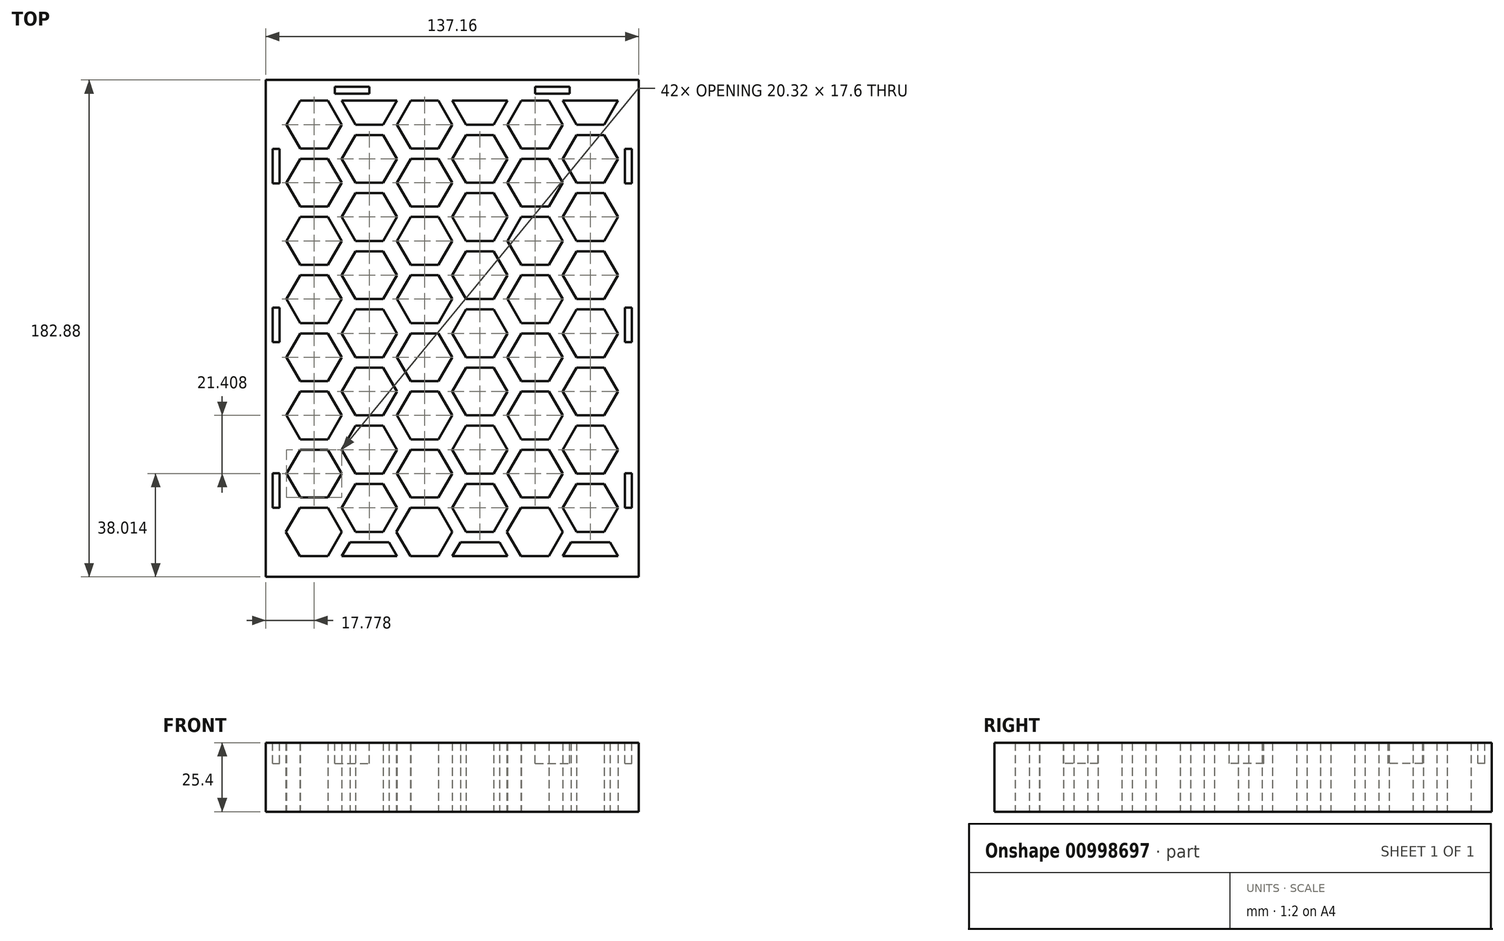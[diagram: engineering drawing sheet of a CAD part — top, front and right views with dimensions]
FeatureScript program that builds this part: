
annotation { "Feature Type Name" : "Feature", "Feature Type Description" : "" }
export const myFeature = defineFeature(function(context is Context, id is Id, definition is map)
    precondition{}
    {
        {
            var Q0;
            Q0=qCreatedBy(makeId("Top.planeOp"),FACE);
            var sketch = newSketch(context, id + "F0", { "sketchPlane" : qUnion([Q0])});
            skLineSegment(sketch, "E0", {"start": v(-64.11, 107.37) * mm, "end": v(-69.2, 98.57) * mm});
            skLineSegment(sketch, "E1", {"start": v(-69.2, 98.57) * mm, "end": v(-64.11, 89.77) * mm});
            skLineSegment(sketch, "E2", {"start": v(-64.11, 89.77) * mm, "end": v(-53.95, 89.77) * mm});
            skLineSegment(sketch, "E3", {"start": v(-53.95, 89.77) * mm, "end": v(-48.87, 98.57) * mm});
            skLineSegment(sketch, "E4", {"start": v(-48.87, 98.57) * mm, "end": v(-53.95, 107.37) * mm});
            skLineSegment(sketch, "E5", {"start": v(-53.95, 107.37) * mm, "end": v(-64.11, 107.37) * mm});
            skLineSegment(sketch, "E6", {"start": v(-64.28, -42.48) * mm, "end": v(-69.41, -51.38) * mm});
            skLineSegment(sketch, "E7", {"start": v(-69.41, -51.38) * mm, "end": v(-64.28, -60.27) * mm});
            skLineSegment(sketch, "E8", {"start": v(-64.28, -60.27) * mm, "end": v(-54, -60.27) * mm});
            skLineSegment(sketch, "E9", {"start": v(-54, -60.27) * mm, "end": v(-48.87, -51.38) * mm});
            skLineSegment(sketch, "E10", {"start": v(-48.87, -51.38) * mm, "end": v(-54, -42.48) * mm});
            skLineSegment(sketch, "E11", {"start": v(-54, -42.48) * mm, "end": v(-64.28, -42.48) * mm});
            skLineSegment(sketch, "E12", {"start": v(-48.87, 107.37) * mm, "end": v(-43.8, 98.57) * mm});
            skLineSegment(sketch, "E13", {"start": v(-43.8, 98.57) * mm, "end": v(-33.63, 98.57) * mm});
            skLineSegment(sketch, "E14", {"start": v(-33.63, 98.57) * mm, "end": v(-28.55, 107.37) * mm});
            skLineSegment(sketch, "E15", {"start": v(-48.87, 107.37) * mm, "end": v(-48.87, -60.27) * mm, "construction": true});
            skLineSegment(sketch, "E16", {"start": v(-43.8, 94.76) * mm, "end": v(-48.87, 85.96) * mm});
            skLineSegment(sketch, "E17", {"start": v(-48.87, 85.96) * mm, "end": v(-43.8, 77.16) * mm});
            skLineSegment(sketch, "E18", {"start": v(-43.8, 77.16) * mm, "end": v(-33.63, 77.16) * mm});
            skLineSegment(sketch, "E19", {"start": v(-33.63, 77.16) * mm, "end": v(-28.55, 85.96) * mm});
            skLineSegment(sketch, "E20", {"start": v(-28.55, 85.96) * mm, "end": v(-33.63, 94.76) * mm});
            skLineSegment(sketch, "E21", {"start": v(-33.63, 94.76) * mm, "end": v(-43.8, 94.76) * mm});
            skLineSegment(sketch, "E22", {"start": v(-43.8, 73.35) * mm, "end": v(-48.87, 64.55) * mm});
            skLineSegment(sketch, "E23", {"start": v(-48.87, 64.55) * mm, "end": v(-43.8, 55.76) * mm});
            skLineSegment(sketch, "E24", {"start": v(-43.8, 55.76) * mm, "end": v(-33.63, 55.76) * mm});
            skLineSegment(sketch, "E25", {"start": v(-33.63, 55.76) * mm, "end": v(-28.55, 64.55) * mm});
            skLineSegment(sketch, "E26", {"start": v(-28.55, 64.55) * mm, "end": v(-33.63, 73.35) * mm});
            skLineSegment(sketch, "E27", {"start": v(-33.63, 73.35) * mm, "end": v(-43.8, 73.35) * mm});
            skLineSegment(sketch, "E28", {"start": v(-43.8, 51.95) * mm, "end": v(-48.87, 43.15) * mm});
            skLineSegment(sketch, "E29", {"start": v(-48.87, 43.15) * mm, "end": v(-43.8, 34.35) * mm});
            skLineSegment(sketch, "E30", {"start": v(-43.8, 34.35) * mm, "end": v(-33.63, 34.35) * mm});
            skLineSegment(sketch, "E31", {"start": v(-33.63, 34.35) * mm, "end": v(-28.55, 43.15) * mm});
            skLineSegment(sketch, "E32", {"start": v(-28.55, 43.15) * mm, "end": v(-33.63, 51.95) * mm});
            skLineSegment(sketch, "E33", {"start": v(-33.63, 51.95) * mm, "end": v(-43.8, 51.95) * mm});
            skLineSegment(sketch, "E34", {"start": v(-43.8, 30.54) * mm, "end": v(-48.87, 21.74) * mm});
            skLineSegment(sketch, "E35", {"start": v(-48.87, 21.74) * mm, "end": v(-43.8, 12.94) * mm});
            skLineSegment(sketch, "E36", {"start": v(-43.8, 12.94) * mm, "end": v(-33.63, 12.94) * mm});
            skLineSegment(sketch, "E37", {"start": v(-33.63, 12.94) * mm, "end": v(-28.55, 21.74) * mm});
            skLineSegment(sketch, "E38", {"start": v(-28.55, 21.74) * mm, "end": v(-33.63, 30.54) * mm});
            skLineSegment(sketch, "E39", {"start": v(-33.63, 30.54) * mm, "end": v(-43.8, 30.54) * mm});
            skLineSegment(sketch, "E40", {"start": v(-43.8, 9.13) * mm, "end": v(-48.87, 0.33) * mm});
            skLineSegment(sketch, "E41", {"start": v(-48.87, 0.33) * mm, "end": v(-43.8, -8.47) * mm});
            skLineSegment(sketch, "E42", {"start": v(-43.8, -8.47) * mm, "end": v(-33.63, -8.47) * mm});
            skLineSegment(sketch, "E43", {"start": v(-33.63, -8.47) * mm, "end": v(-28.55, 0.33) * mm});
            skLineSegment(sketch, "E44", {"start": v(-28.55, 0.33) * mm, "end": v(-33.63, 9.13) * mm});
            skLineSegment(sketch, "E45", {"start": v(-33.63, 9.13) * mm, "end": v(-43.8, 9.13) * mm});
            skLineSegment(sketch, "E46", {"start": v(-43.8, -12.28) * mm, "end": v(-48.87, -21.08) * mm});
            skLineSegment(sketch, "E47", {"start": v(-48.87, -21.08) * mm, "end": v(-43.8, -29.88) * mm});
            skLineSegment(sketch, "E48", {"start": v(-43.8, -29.88) * mm, "end": v(-33.63, -29.88) * mm});
            skLineSegment(sketch, "E49", {"start": v(-33.63, -29.88) * mm, "end": v(-28.55, -21.08) * mm});
            skLineSegment(sketch, "E50", {"start": v(-28.55, -21.08) * mm, "end": v(-33.63, -12.28) * mm});
            skLineSegment(sketch, "E51", {"start": v(-33.63, -12.28) * mm, "end": v(-43.8, -12.28) * mm});
            skLineSegment(sketch, "E52", {"start": v(-43.8, -33.69) * mm, "end": v(-48.87, -42.48) * mm});
            skLineSegment(sketch, "E53", {"start": v(-48.87, -42.48) * mm, "end": v(-43.8, -51.28) * mm});
            skLineSegment(sketch, "E54", {"start": v(-43.8, -51.28) * mm, "end": v(-33.63, -51.28) * mm});
            skLineSegment(sketch, "E55", {"start": v(-33.63, -51.28) * mm, "end": v(-28.55, -42.48) * mm});
            skLineSegment(sketch, "E56", {"start": v(-28.55, -42.48) * mm, "end": v(-33.63, -33.69) * mm});
            skLineSegment(sketch, "E57", {"start": v(-33.63, -33.69) * mm, "end": v(-43.8, -33.69) * mm});
            skLineSegment(sketch, "E58", {"start": v(-45.88, -55.1) * mm, "end": v(-48.87, -60.27) * mm});
            skLineSegment(sketch, "E59", {"start": v(-28.55, -60.27) * mm, "end": v(-31.54, -55.1) * mm});
            skLineSegment(sketch, "E60", {"start": v(-31.54, -55.1) * mm, "end": v(-45.88, -55.1) * mm});
            skLineSegment(sketch, "E61", {"start": v(-28.55, 107.37) * mm, "end": v(-28.55, -60.27) * mm, "construction": true});
            skLineSegment(sketch, "E62", {"start": v(-23.47, 107.37) * mm, "end": v(-28.55, 98.57) * mm});
            skLineSegment(sketch, "E63", {"start": v(-28.55, 98.57) * mm, "end": v(-23.47, 89.77) * mm});
            skLineSegment(sketch, "E64", {"start": v(-23.47, 89.77) * mm, "end": v(-13.31, 89.77) * mm});
            skLineSegment(sketch, "E65", {"start": v(-13.31, 89.77) * mm, "end": v(-8.23, 98.57) * mm});
            skLineSegment(sketch, "E66", {"start": v(-8.23, 98.57) * mm, "end": v(-13.31, 107.37) * mm});
            skLineSegment(sketch, "E67", {"start": v(-13.31, 107.37) * mm, "end": v(-23.47, 107.37) * mm});
            skLineSegment(sketch, "E68", {"start": v(-23.47, 85.96) * mm, "end": v(-28.55, 77.16) * mm});
            skLineSegment(sketch, "E69", {"start": v(-28.55, 77.16) * mm, "end": v(-23.47, 68.36) * mm});
            skLineSegment(sketch, "E70", {"start": v(-23.47, 68.36) * mm, "end": v(-13.31, 68.36) * mm});
            skLineSegment(sketch, "E71", {"start": v(-13.31, 68.36) * mm, "end": v(-8.23, 77.16) * mm});
            skLineSegment(sketch, "E72", {"start": v(-8.23, 77.16) * mm, "end": v(-13.31, 85.96) * mm});
            skLineSegment(sketch, "E73", {"start": v(-13.31, 85.96) * mm, "end": v(-23.47, 85.96) * mm});
            skLineSegment(sketch, "E74", {"start": v(-23.47, 43.15) * mm, "end": v(-28.55, 34.35) * mm});
            skLineSegment(sketch, "E75", {"start": v(-28.55, 34.35) * mm, "end": v(-23.47, 25.55) * mm});
            skLineSegment(sketch, "E76", {"start": v(-23.47, 25.55) * mm, "end": v(-13.31, 25.55) * mm});
            skLineSegment(sketch, "E77", {"start": v(-13.31, 25.55) * mm, "end": v(-8.23, 34.35) * mm});
            skLineSegment(sketch, "E78", {"start": v(-8.23, 34.35) * mm, "end": v(-13.31, 43.15) * mm});
            skLineSegment(sketch, "E79", {"start": v(-13.31, 43.15) * mm, "end": v(-23.47, 43.15) * mm});
            skLineSegment(sketch, "E80", {"start": v(-23.47, 21.74) * mm, "end": v(-28.55, 12.94) * mm});
            skLineSegment(sketch, "E81", {"start": v(-28.55, 12.94) * mm, "end": v(-23.47, 4.14) * mm});
            skLineSegment(sketch, "E82", {"start": v(-23.47, 4.14) * mm, "end": v(-13.31, 4.14) * mm});
            skLineSegment(sketch, "E83", {"start": v(-13.31, 4.14) * mm, "end": v(-8.23, 12.94) * mm});
            skLineSegment(sketch, "E84", {"start": v(-8.23, 12.94) * mm, "end": v(-13.31, 21.74) * mm});
            skLineSegment(sketch, "E85", {"start": v(-13.31, 21.74) * mm, "end": v(-23.47, 21.74) * mm});
            skLineSegment(sketch, "E86", {"start": v(-23.47, 64.55) * mm, "end": v(-28.55, 55.76) * mm});
            skLineSegment(sketch, "E87", {"start": v(-28.55, 55.76) * mm, "end": v(-23.47, 46.96) * mm});
            skLineSegment(sketch, "E88", {"start": v(-23.47, 46.96) * mm, "end": v(-13.31, 46.96) * mm});
            skLineSegment(sketch, "E89", {"start": v(-13.31, 46.96) * mm, "end": v(-8.23, 55.76) * mm});
            skLineSegment(sketch, "E90", {"start": v(-8.23, 55.76) * mm, "end": v(-13.31, 64.55) * mm});
            skLineSegment(sketch, "E91", {"start": v(-13.31, 64.55) * mm, "end": v(-23.47, 64.55) * mm});
            skLineSegment(sketch, "E92", {"start": v(-23.47, 0.33) * mm, "end": v(-28.55, -8.47) * mm});
            skLineSegment(sketch, "E93", {"start": v(-28.55, -8.47) * mm, "end": v(-23.47, -17.27) * mm});
            skLineSegment(sketch, "E94", {"start": v(-23.47, -17.27) * mm, "end": v(-13.31, -17.27) * mm});
            skLineSegment(sketch, "E95", {"start": v(-13.31, -17.27) * mm, "end": v(-8.23, -8.47) * mm});
            skLineSegment(sketch, "E96", {"start": v(-8.23, -8.47) * mm, "end": v(-13.31, 0.33) * mm});
            skLineSegment(sketch, "E97", {"start": v(-13.31, 0.33) * mm, "end": v(-23.47, 0.33) * mm});
            skLineSegment(sketch, "E98", {"start": v(-23.47, -21.08) * mm, "end": v(-28.55, -29.88) * mm});
            skLineSegment(sketch, "E99", {"start": v(-28.55, -29.88) * mm, "end": v(-23.47, -38.67) * mm});
            skLineSegment(sketch, "E100", {"start": v(-23.47, -38.67) * mm, "end": v(-13.31, -38.67) * mm});
            skLineSegment(sketch, "E101", {"start": v(-13.31, -38.67) * mm, "end": v(-8.23, -29.88) * mm});
            skLineSegment(sketch, "E102", {"start": v(-8.23, -29.88) * mm, "end": v(-13.31, -21.08) * mm});
            skLineSegment(sketch, "E103", {"start": v(-13.31, -21.08) * mm, "end": v(-23.47, -21.08) * mm});
            skLineSegment(sketch, "E104", {"start": v(-23.64, -42.48) * mm, "end": v(-28.77, -51.38) * mm});
            skLineSegment(sketch, "E105", {"start": v(-28.77, -51.38) * mm, "end": v(-23.64, -60.27) * mm});
            skLineSegment(sketch, "E106", {"start": v(-23.64, -60.27) * mm, "end": v(-13.37, -60.27) * mm});
            skLineSegment(sketch, "E107", {"start": v(-13.37, -60.27) * mm, "end": v(-8.23, -51.38) * mm});
            skLineSegment(sketch, "E108", {"start": v(-8.23, -51.38) * mm, "end": v(-13.37, -42.48) * mm});
            skLineSegment(sketch, "E109", {"start": v(-13.37, -42.48) * mm, "end": v(-23.64, -42.48) * mm});
            skLineSegment(sketch, "E110", {"start": v(-8.23, 107.37) * mm, "end": v(-3.15, 98.57) * mm});
            skLineSegment(sketch, "E111", {"start": v(-3.15, 98.57) * mm, "end": v(7, 98.57) * mm});
            skLineSegment(sketch, "E112", {"start": v(7, 98.57) * mm, "end": v(12.09, 107.37) * mm});
            skLineSegment(sketch, "E113", {"start": v(-8.23, 107.37) * mm, "end": v(-8.23, -60.27) * mm, "construction": true});
            skLineSegment(sketch, "E114", {"start": v(-3.15, 94.76) * mm, "end": v(-8.23, 85.96) * mm});
            skLineSegment(sketch, "E115", {"start": v(-8.23, 85.96) * mm, "end": v(-3.15, 77.16) * mm});
            skLineSegment(sketch, "E116", {"start": v(-3.15, 77.16) * mm, "end": v(7, 77.16) * mm});
            skLineSegment(sketch, "E117", {"start": v(7, 77.16) * mm, "end": v(12.09, 85.96) * mm});
            skLineSegment(sketch, "E118", {"start": v(12.09, 85.96) * mm, "end": v(7, 94.76) * mm});
            skLineSegment(sketch, "E119", {"start": v(7, 94.76) * mm, "end": v(-3.15, 94.76) * mm});
            skLineSegment(sketch, "E120", {"start": v(-3.15, 73.35) * mm, "end": v(-8.23, 64.55) * mm});
            skLineSegment(sketch, "E121", {"start": v(-8.23, 64.55) * mm, "end": v(-3.15, 55.76) * mm});
            skLineSegment(sketch, "E122", {"start": v(-3.15, 55.76) * mm, "end": v(7, 55.76) * mm});
            skLineSegment(sketch, "E123", {"start": v(7, 55.76) * mm, "end": v(12.09, 64.55) * mm});
            skLineSegment(sketch, "E124", {"start": v(12.09, 64.55) * mm, "end": v(7, 73.35) * mm});
            skLineSegment(sketch, "E125", {"start": v(7, 73.35) * mm, "end": v(-3.15, 73.35) * mm});
            skLineSegment(sketch, "E126", {"start": v(-3.15, 51.95) * mm, "end": v(-8.23, 43.15) * mm});
            skLineSegment(sketch, "E127", {"start": v(-8.23, 43.15) * mm, "end": v(-3.15, 34.35) * mm});
            skLineSegment(sketch, "E128", {"start": v(-3.15, 34.35) * mm, "end": v(7, 34.35) * mm});
            skLineSegment(sketch, "E129", {"start": v(7, 34.35) * mm, "end": v(12.09, 43.15) * mm});
            skLineSegment(sketch, "E130", {"start": v(12.09, 43.15) * mm, "end": v(7, 51.95) * mm});
            skLineSegment(sketch, "E131", {"start": v(7, 51.95) * mm, "end": v(-3.15, 51.95) * mm});
            skLineSegment(sketch, "E132", {"start": v(-3.15, 30.54) * mm, "end": v(-8.23, 21.74) * mm});
            skLineSegment(sketch, "E133", {"start": v(-8.23, 21.74) * mm, "end": v(-3.15, 12.94) * mm});
            skLineSegment(sketch, "E134", {"start": v(-3.15, 12.94) * mm, "end": v(7, 12.94) * mm});
            skLineSegment(sketch, "E135", {"start": v(7, 12.94) * mm, "end": v(12.09, 21.74) * mm});
            skLineSegment(sketch, "E136", {"start": v(12.09, 21.74) * mm, "end": v(7, 30.54) * mm});
            skLineSegment(sketch, "E137", {"start": v(7, 30.54) * mm, "end": v(-3.15, 30.54) * mm});
            skLineSegment(sketch, "E138", {"start": v(-3.15, 9.13) * mm, "end": v(-8.23, 0.33) * mm});
            skLineSegment(sketch, "E139", {"start": v(-8.23, 0.33) * mm, "end": v(-3.15, -8.47) * mm});
            skLineSegment(sketch, "E140", {"start": v(-3.15, -8.47) * mm, "end": v(7, -8.47) * mm});
            skLineSegment(sketch, "E141", {"start": v(7, -8.47) * mm, "end": v(12.09, 0.33) * mm});
            skLineSegment(sketch, "E142", {"start": v(12.09, 0.33) * mm, "end": v(7, 9.13) * mm});
            skLineSegment(sketch, "E143", {"start": v(7, 9.13) * mm, "end": v(-3.15, 9.13) * mm});
            skLineSegment(sketch, "E144", {"start": v(-3.15, -12.28) * mm, "end": v(-8.23, -21.08) * mm});
            skLineSegment(sketch, "E145", {"start": v(-8.23, -21.08) * mm, "end": v(-3.15, -29.88) * mm});
            skLineSegment(sketch, "E146", {"start": v(-3.15, -29.88) * mm, "end": v(7, -29.88) * mm});
            skLineSegment(sketch, "E147", {"start": v(7, -29.88) * mm, "end": v(12.09, -21.08) * mm});
            skLineSegment(sketch, "E148", {"start": v(12.09, -21.08) * mm, "end": v(7, -12.28) * mm});
            skLineSegment(sketch, "E149", {"start": v(7, -12.28) * mm, "end": v(-3.15, -12.28) * mm});
            skLineSegment(sketch, "E150", {"start": v(-3.15, -33.69) * mm, "end": v(-8.23, -42.48) * mm});
            skLineSegment(sketch, "E151", {"start": v(-8.23, -42.48) * mm, "end": v(-3.15, -51.28) * mm});
            skLineSegment(sketch, "E152", {"start": v(-3.15, -51.28) * mm, "end": v(7, -51.28) * mm});
            skLineSegment(sketch, "E153", {"start": v(7, -51.28) * mm, "end": v(12.09, -42.48) * mm});
            skLineSegment(sketch, "E154", {"start": v(12.09, -42.48) * mm, "end": v(7, -33.69) * mm});
            skLineSegment(sketch, "E155", {"start": v(7, -33.69) * mm, "end": v(-3.15, -33.69) * mm});
            skLineSegment(sketch, "E156", {"start": v(-5.24, -55.1) * mm, "end": v(-8.23, -60.27) * mm});
            skLineSegment(sketch, "E157", {"start": v(12.09, -60.27) * mm, "end": v(9.1, -55.1) * mm});
            skLineSegment(sketch, "E158", {"start": v(9.1, -55.1) * mm, "end": v(-5.24, -55.1) * mm});
            skLineSegment(sketch, "E159", {"start": v(12.09, 107.37) * mm, "end": v(12.09, -60.27) * mm, "construction": true});
            skLineSegment(sketch, "E160", {"start": v(-69.2, 107.37) * mm, "end": v(52.73, 107.37) * mm, "construction": true});
            skLineSegment(sketch, "E161", {"start": v(17.17, 107.37) * mm, "end": v(12.09, 98.57) * mm});
            skLineSegment(sketch, "E162", {"start": v(12.09, 98.57) * mm, "end": v(17.17, 89.77) * mm});
            skLineSegment(sketch, "E163", {"start": v(17.17, 89.77) * mm, "end": v(27.33, 89.77) * mm});
            skLineSegment(sketch, "E164", {"start": v(27.33, 89.77) * mm, "end": v(32.4, 98.57) * mm});
            skLineSegment(sketch, "E165", {"start": v(32.4, 98.57) * mm, "end": v(27.33, 107.37) * mm});
            skLineSegment(sketch, "E166", {"start": v(27.33, 107.37) * mm, "end": v(17.17, 107.37) * mm});
            skLineSegment(sketch, "E167", {"start": v(17.17, 85.96) * mm, "end": v(12.09, 77.16) * mm});
            skLineSegment(sketch, "E168", {"start": v(12.09, 77.16) * mm, "end": v(17.17, 68.36) * mm});
            skLineSegment(sketch, "E169", {"start": v(17.17, 68.36) * mm, "end": v(27.33, 68.36) * mm});
            skLineSegment(sketch, "E170", {"start": v(27.33, 68.36) * mm, "end": v(32.4, 77.16) * mm});
            skLineSegment(sketch, "E171", {"start": v(32.4, 77.16) * mm, "end": v(27.33, 85.96) * mm});
            skLineSegment(sketch, "E172", {"start": v(27.33, 85.96) * mm, "end": v(17.17, 85.96) * mm});
            skLineSegment(sketch, "E173", {"start": v(17.17, 43.15) * mm, "end": v(12.09, 34.35) * mm});
            skLineSegment(sketch, "E174", {"start": v(12.09, 34.35) * mm, "end": v(17.17, 25.55) * mm});
            skLineSegment(sketch, "E175", {"start": v(17.17, 25.55) * mm, "end": v(27.33, 25.55) * mm});
            skLineSegment(sketch, "E176", {"start": v(27.33, 25.55) * mm, "end": v(32.4, 34.35) * mm});
            skLineSegment(sketch, "E177", {"start": v(32.4, 34.35) * mm, "end": v(27.33, 43.15) * mm});
            skLineSegment(sketch, "E178", {"start": v(27.33, 43.15) * mm, "end": v(17.17, 43.15) * mm});
            skLineSegment(sketch, "E179", {"start": v(17.17, 21.74) * mm, "end": v(12.09, 12.94) * mm});
            skLineSegment(sketch, "E180", {"start": v(12.09, 12.94) * mm, "end": v(17.17, 4.14) * mm});
            skLineSegment(sketch, "E181", {"start": v(17.17, 4.14) * mm, "end": v(27.33, 4.14) * mm});
            skLineSegment(sketch, "E182", {"start": v(27.33, 4.14) * mm, "end": v(32.4, 12.94) * mm});
            skLineSegment(sketch, "E183", {"start": v(32.4, 12.94) * mm, "end": v(27.33, 21.74) * mm});
            skLineSegment(sketch, "E184", {"start": v(27.33, 21.74) * mm, "end": v(17.17, 21.74) * mm});
            skLineSegment(sketch, "E185", {"start": v(17.17, 64.55) * mm, "end": v(12.09, 55.76) * mm});
            skLineSegment(sketch, "E186", {"start": v(12.09, 55.76) * mm, "end": v(17.17, 46.96) * mm});
            skLineSegment(sketch, "E187", {"start": v(17.17, 46.96) * mm, "end": v(27.33, 46.96) * mm});
            skLineSegment(sketch, "E188", {"start": v(27.33, 46.96) * mm, "end": v(32.4, 55.76) * mm});
            skLineSegment(sketch, "E189", {"start": v(32.4, 55.76) * mm, "end": v(27.33, 64.55) * mm});
            skLineSegment(sketch, "E190", {"start": v(27.33, 64.55) * mm, "end": v(17.17, 64.55) * mm});
            skLineSegment(sketch, "E191", {"start": v(17.17, 0.33) * mm, "end": v(12.09, -8.47) * mm});
            skLineSegment(sketch, "E192", {"start": v(12.09, -8.47) * mm, "end": v(17.17, -17.27) * mm});
            skLineSegment(sketch, "E193", {"start": v(17.17, -17.27) * mm, "end": v(27.33, -17.27) * mm});
            skLineSegment(sketch, "E194", {"start": v(27.33, -17.27) * mm, "end": v(32.4, -8.47) * mm});
            skLineSegment(sketch, "E195", {"start": v(32.4, -8.47) * mm, "end": v(27.33, 0.33) * mm});
            skLineSegment(sketch, "E196", {"start": v(27.33, 0.33) * mm, "end": v(17.17, 0.33) * mm});
            skLineSegment(sketch, "E197", {"start": v(17.17, -21.08) * mm, "end": v(12.09, -29.88) * mm});
            skLineSegment(sketch, "E198", {"start": v(12.09, -29.88) * mm, "end": v(17.17, -38.67) * mm});
            skLineSegment(sketch, "E199", {"start": v(17.17, -38.67) * mm, "end": v(27.33, -38.67) * mm});
            skLineSegment(sketch, "E200", {"start": v(27.33, -38.67) * mm, "end": v(32.4, -29.88) * mm});
            skLineSegment(sketch, "E201", {"start": v(32.4, -29.88) * mm, "end": v(27.33, -21.08) * mm});
            skLineSegment(sketch, "E202", {"start": v(27.33, -21.08) * mm, "end": v(17.17, -21.08) * mm});
            skLineSegment(sketch, "E203", {"start": v(17, -42.48) * mm, "end": v(11.87, -51.38) * mm});
            skLineSegment(sketch, "E204", {"start": v(11.87, -51.38) * mm, "end": v(17, -60.27) * mm});
            skLineSegment(sketch, "E205", {"start": v(17, -60.27) * mm, "end": v(27.27, -60.27) * mm});
            skLineSegment(sketch, "E206", {"start": v(27.27, -60.27) * mm, "end": v(32.4, -51.38) * mm});
            skLineSegment(sketch, "E207", {"start": v(32.4, -51.38) * mm, "end": v(27.27, -42.48) * mm});
            skLineSegment(sketch, "E208", {"start": v(27.27, -42.48) * mm, "end": v(17, -42.48) * mm});
            skLineSegment(sketch, "E209", {"start": v(32.4, 107.37) * mm, "end": v(37.49, 98.57) * mm});
            skLineSegment(sketch, "E210", {"start": v(37.49, 98.57) * mm, "end": v(47.65, 98.57) * mm});
            skLineSegment(sketch, "E211", {"start": v(47.65, 98.57) * mm, "end": v(52.73, 107.37) * mm});
            skLineSegment(sketch, "E212", {"start": v(32.4, 107.37) * mm, "end": v(32.4, -60.27) * mm, "construction": true});
            skLineSegment(sketch, "E213", {"start": v(35.4, -55.1) * mm, "end": v(32.4, -60.27) * mm});
            skLineSegment(sketch, "E214", {"start": v(52.73, -60.27) * mm, "end": v(49.74, -55.1) * mm});
            skLineSegment(sketch, "E215", {"start": v(49.74, -55.1) * mm, "end": v(35.4, -55.1) * mm});
            skLineSegment(sketch, "E216", {"start": v(52.73, 107.37) * mm, "end": v(52.73, -60.27) * mm, "construction": true});
            skLineSegment(sketch, "E217", {"start": v(52.73, -60.27) * mm, "end": v(-69.2, -60.27) * mm, "construction": true});
            skLineSegment(sketch, "E218", {"start": v(-69.2, -60.27) * mm, "end": v(-69.2, 107.37) * mm, "construction": true});
            skLineSegment(sketch, "E219.bottom", {"start": v(-76.81, 114.99) * mm, "end": v(60.35, 114.99) * mm});
            skLineSegment(sketch, "E219.top", {"start": v(-76.81, -67.9) * mm, "end": v(60.35, -67.9) * mm});
            skLineSegment(sketch, "E219.left", {"start": v(-76.81, 114.99) * mm, "end": v(-76.81, -67.9) * mm});
            skLineSegment(sketch, "E219.right", {"start": v(60.35, 114.99) * mm, "end": v(60.35, -67.9) * mm});
            skLineSegment(sketch, "E220.bottom", {"start": v(-73, 111.18) * mm, "end": v(56.54, 111.18) * mm});
            skLineSegment(sketch, "E220.top", {"start": v(-73, -67.9) * mm, "end": v(56.54, -67.9) * mm});
            skLineSegment(sketch, "E220.left", {"start": v(-73, 111.18) * mm, "end": v(-73, -67.9) * mm});
            skLineSegment(sketch, "E220.right", {"start": v(56.54, 111.18) * mm, "end": v(56.54, -67.9) * mm});
            skLineSegment(sketch, "E221", {"start": v(32.4, -60.27) * mm, "end": v(52.73, -60.27) * mm});
            skLineSegment(sketch, "E222", {"start": v(-8.23, -60.27) * mm, "end": v(12.09, -60.27) * mm});
            skLineSegment(sketch, "E223", {"start": v(32.4, 107.37) * mm, "end": v(52.73, 107.37) * mm});
            skLineSegment(sketch, "E224", {"start": v(12.09, 107.37) * mm, "end": v(-8.23, 107.37) * mm});
            skLineSegment(sketch, "E225", {"start": v(-28.55, 107.37) * mm, "end": v(-48.87, 107.37) * mm});
            skLineSegment(sketch, "E226", {"start": v(-48.87, -60.27) * mm, "end": v(-28.55, -60.27) * mm});
            skSolve(sketch);
        }
        {
            var Q0;
            Q0=makeQuery(id+"F0.imprint","IMPRINT",FACE,{"disambiguationData":[TD([[makeQuery(id+"F0.imprint","IMPRINT",EDGE,{"derivedFrom":sQuery(id+"F0.wireOp",EDGE,"a3d6729a-a9fa-40fb-8c57-60344376bb60")}),1.0]])]});
            var Q1;
            Q1=makeQuery(id+"F0.imprint","IMPRINT",FACE,{"disambiguationData":[TD([[makeQuery(id+"F0.imprint","IMPRINT",EDGE,{"derivedFrom":sQuery(id+"F0.wireOp",EDGE,"36840c81-68fc-456b-b918-5e75b1f56573")}),1.0]])]});
            var Q2;
            Q2=makeQuery(id+"F0.imprint","IMPRINT",FACE,{"disambiguationData":[TD([[makeQuery(id+"F0.imprint","IMPRINT",EDGE,{"derivedFrom":sQuery(id+"F0.wireOp",EDGE,"b8766c8d-9eda-4f00-b00c-fb24c00b1e0d")}),1.0]])]});
            var Q3;
            Q3=makeQuery(id+"F0.imprint","IMPRINT",FACE,{"disambiguationData":[TD([[makeQuery(id+"F0.imprint","IMPRINT",EDGE,{"derivedFrom":sQuery(id+"F0.wireOp",EDGE,"E28")}),1.0]])]});
            var Q4;
            Q4=makeQuery(id+"F0.imprint","IMPRINT",FACE,{"disambiguationData":[TD([[makeQuery(id+"F0.imprint","IMPRINT",EDGE,{"derivedFrom":sQuery(id+"F0.wireOp",EDGE,"E74")}),1.0]])]});
            var Q5;
            Q5=makeQuery(id+"F0.imprint","IMPRINT",FACE,{"disambiguationData":[TD([[makeQuery(id+"F0.imprint","IMPRINT",EDGE,{"derivedFrom":sQuery(id+"F0.wireOp",EDGE,"E80")}),1.0]])]});
            var Q6;
            Q6=makeQuery(id+"F0.imprint","IMPRINT",FACE,{"disambiguationData":[TD([[makeQuery(id+"F0.imprint","IMPRINT",EDGE,{"derivedFrom":sQuery(id+"F0.wireOp",EDGE,"E92")}),1.0]])]});
            var Q7;
            Q7=makeQuery(id+"F0.imprint","IMPRINT",FACE,{"disambiguationData":[TD([[makeQuery(id+"F0.imprint","IMPRINT",EDGE,{"derivedFrom":sQuery(id+"F0.wireOp",EDGE,"E46")}),1.0]])]});
            var Q8;
            Q8=makeQuery(id+"F0.imprint","IMPRINT",FACE,{"disambiguationData":[TD([[makeQuery(id+"F0.imprint","IMPRINT",EDGE,{"derivedFrom":sQuery(id+"F0.wireOp",EDGE,"f9f120df-92e4-45f2-acea-5ec26f3b381e")}),1.0]])]});
            var Q9;
            Q9=makeQuery(id+"F0.imprint","IMPRINT",FACE,{"disambiguationData":[TD([[makeQuery(id+"F0.imprint","IMPRINT",EDGE,{"derivedFrom":sQuery(id+"F0.wireOp",EDGE,"E98")}),1.0]])]});
            var Q10;
            Q10=makeQuery(id+"F0.imprint","IMPRINT",FACE,{"disambiguationData":[TD([[makeQuery(id+"F0.imprint","IMPRINT",EDGE,{"derivedFrom":sQuery(id+"F0.wireOp",EDGE,"E52")}),1.0]])]});
            var Q11;
            Q11=makeQuery(id+"F0.imprint","IMPRINT",FACE,{"disambiguationData":[TD([[makeQuery(id+"F0.imprint","IMPRINT",EDGE,{"derivedFrom":sQuery(id+"F0.wireOp",EDGE,"E144")}),1.0]])]});
            var Q12;
            Q12=makeQuery(id+"F0.imprint","IMPRINT",FACE,{"disambiguationData":[TD([[makeQuery(id+"F0.imprint","IMPRINT",EDGE,{"derivedFrom":sQuery(id+"F0.wireOp",EDGE,"E138")}),1.0]])]});
            var Q13;
            Q13=makeQuery(id+"F0.imprint","IMPRINT",FACE,{"disambiguationData":[TD([[makeQuery(id+"F0.imprint","IMPRINT",EDGE,{"derivedFrom":sQuery(id+"F0.wireOp",EDGE,"E191")}),1.0]])]});
            var Q14;
            Q14=makeQuery(id+"F0.imprint","IMPRINT",FACE,{"disambiguationData":[TD([[makeQuery(id+"F0.imprint","IMPRINT",EDGE,{"derivedFrom":sQuery(id+"F0.wireOp",EDGE,"E197")}),1.0]])]});
            var Q15;
            Q15=makeQuery(id+"F0.imprint","IMPRINT",FACE,{"disambiguationData":[TD([[makeQuery(id+"F0.imprint","IMPRINT",EDGE,{"derivedFrom":sQuery(id+"F0.wireOp",EDGE,"c88cee6e-aa33-4b70-82b9-259b2a569ca4")}),1.0]])]});
            var Q16;
            Q16=makeQuery(id+"F0.imprint","IMPRINT",FACE,{"disambiguationData":[TD([[makeQuery(id+"F0.imprint","IMPRINT",EDGE,{"derivedFrom":sQuery(id+"F0.wireOp",EDGE,"3aa0dbc3-910e-427b-94b0-181b511888f7")}),1.0]])]});
            var Q17;
            Q17=makeQuery(id+"F0.imprint","IMPRINT",FACE,{"disambiguationData":[TD([[makeQuery(id+"F0.imprint","IMPRINT",EDGE,{"derivedFrom":sQuery(id+"F0.wireOp",EDGE,"E179")}),1.0]])]});
            var Q18;
            Q18=makeQuery(id+"F0.imprint","IMPRINT",FACE,{"disambiguationData":[TD([[makeQuery(id+"F0.imprint","IMPRINT",EDGE,{"derivedFrom":sQuery(id+"F0.wireOp",EDGE,"34189966-8765-4ee0-a042-d8a498b5a9f3")}),1.0]])]});
            var Q19;
            Q19=makeQuery(id+"F0.imprint","IMPRINT",FACE,{"disambiguationData":[TD([[makeQuery(id+"F0.imprint","IMPRINT",EDGE,{"derivedFrom":sQuery(id+"F0.wireOp",EDGE,"E132")}),1.0]])]});
            var Q20;
            Q20=makeQuery(id+"F0.imprint","IMPRINT",FACE,{"disambiguationData":[TD([[makeQuery(id+"F0.imprint","IMPRINT",EDGE,{"derivedFrom":sQuery(id+"F0.wireOp",EDGE,"E173")}),1.0]])]});
            var Q21;
            Q21=makeQuery(id+"F0.imprint","IMPRINT",FACE,{"disambiguationData":[TD([[makeQuery(id+"F0.imprint","IMPRINT",EDGE,{"derivedFrom":sQuery(id+"F0.wireOp",EDGE,"E126")}),1.0]])]});
            var Q22;
            Q22=makeQuery(id+"F0.imprint","IMPRINT",FACE,{"disambiguationData":[TD([[makeQuery(id+"F0.imprint","IMPRINT",EDGE,{"derivedFrom":sQuery(id+"F0.wireOp",EDGE,"aeeefb6b-7289-4e22-b0eb-735a70cf45d1")}),1.0]])]});
            var Q23;
            Q23=makeQuery(id+"F0.imprint","IMPRINT",FACE,{"disambiguationData":[TD([[makeQuery(id+"F0.imprint","IMPRINT",EDGE,{"derivedFrom":sQuery(id+"F0.wireOp",EDGE,"E185")}),1.0]])]});
            var Q24;
            Q24=makeQuery(id+"F0.imprint","IMPRINT",FACE,{"disambiguationData":[TD([[makeQuery(id+"F0.imprint","IMPRINT",EDGE,{"derivedFrom":sQuery(id+"F0.wireOp",EDGE,"0e9159b1-e5b5-4a6d-a294-257f092bd98a")}),1.0]])]});
            var Q25;
            Q25=makeQuery(id+"F0.imprint","IMPRINT",FACE,{"disambiguationData":[TD([[makeQuery(id+"F0.imprint","IMPRINT",EDGE,{"derivedFrom":sQuery(id+"F0.wireOp",EDGE,"E120")}),1.0]])]});
            var Q26;
            Q26=makeQuery(id+"F0.imprint","IMPRINT",FACE,{"disambiguationData":[TD([[makeQuery(id+"F0.imprint","IMPRINT",EDGE,{"derivedFrom":sQuery(id+"F0.wireOp",EDGE,"E86")}),1.0]])]});
            var Q27;
            Q27=makeQuery(id+"F0.imprint","IMPRINT",FACE,{"disambiguationData":[TD([[makeQuery(id+"F0.imprint","IMPRINT",EDGE,{"derivedFrom":sQuery(id+"F0.wireOp",EDGE,"E22")}),1.0]])]});
            var Q28;
            Q28=makeQuery(id+"F0.imprint","IMPRINT",FACE,{"disambiguationData":[TD([[makeQuery(id+"F0.imprint","IMPRINT",EDGE,{"derivedFrom":sQuery(id+"F0.wireOp",EDGE,"09709f0e-1614-4ce7-a8c8-38e27e8c5e23")}),1.0]])]});
            var Q29;
            Q29=makeQuery(id+"F0.imprint","IMPRINT",FACE,{"disambiguationData":[TD([[makeQuery(id+"F0.imprint","IMPRINT",EDGE,{"derivedFrom":sQuery(id+"F0.wireOp",EDGE,"f900e705-0d34-45c1-b6ed-51a550f8fed7")}),1.0]])]});
            var Q30;
            Q30=makeQuery(id+"F0.imprint","IMPRINT",FACE,{"disambiguationData":[TD([[makeQuery(id+"F0.imprint","IMPRINT",EDGE,{"derivedFrom":sQuery(id+"F0.wireOp",EDGE,"E16")}),1.0]])]});
            var Q31;
            Q31=makeQuery(id+"F0.imprint","IMPRINT",FACE,{"disambiguationData":[TD([[makeQuery(id+"F0.imprint","IMPRINT",EDGE,{"derivedFrom":sQuery(id+"F0.wireOp",EDGE,"E68")}),1.0]])]});
            var Q32;
            Q32=makeQuery(id+"F0.imprint","IMPRINT",FACE,{"disambiguationData":[TD([[makeQuery(id+"F0.imprint","IMPRINT",EDGE,{"derivedFrom":sQuery(id+"F0.wireOp",EDGE,"E114")}),1.0]])]});
            var Q33;
            Q33=makeQuery(id+"F0.imprint","IMPRINT",FACE,{"disambiguationData":[TD([[makeQuery(id+"F0.imprint","IMPRINT",EDGE,{"derivedFrom":sQuery(id+"F0.wireOp",EDGE,"E167")}),1.0]])]});
            var Q34;
            Q34=makeQuery(id+"F0.imprint","IMPRINT",FACE,{"disambiguationData":[TD([[makeQuery(id+"F0.imprint","IMPRINT",EDGE,{"derivedFrom":sQuery(id+"F0.wireOp",EDGE,"f47d0d4d-eeff-4b28-b0e7-2e7193aa36ea")}),1.0]])]});
            var Q35;
            Q35=makeQuery(id+"F0.imprint","IMPRINT",FACE,{"disambiguationData":[TD([[makeQuery(id+"F0.imprint","IMPRINT",EDGE,{"derivedFrom":sQuery(id+"F0.wireOp",EDGE,"E213")}),1.0]])]});
            var Q36;
            Q36=makeQuery(id+"F0.imprint","IMPRINT",FACE,{"disambiguationData":[TD([[makeQuery(id+"F0.imprint","IMPRINT",EDGE,{"derivedFrom":sQuery(id+"F0.wireOp",EDGE,"fc479316-7fc6-4818-8bd3-e6f60e8cae3a")}),1.0]])]});
            var Q37;
            Q37=makeQuery(id+"F0.imprint","IMPRINT",FACE,{"disambiguationData":[TD([[makeQuery(id+"F0.imprint","IMPRINT",EDGE,{"derivedFrom":sQuery(id+"F0.wireOp",EDGE,"E203")}),1.0]])]});
            var Q38;
            Q38=makeQuery(id+"F0.imprint","IMPRINT",FACE,{"disambiguationData":[TD([[makeQuery(id+"F0.imprint","IMPRINT",EDGE,{"derivedFrom":sQuery(id+"F0.wireOp",EDGE,"E150")}),1.0]])]});
            var Q39;
            Q39=makeQuery(id+"F0.imprint","IMPRINT",FACE,{"disambiguationData":[TD([[makeQuery(id+"F0.imprint","IMPRINT",EDGE,{"derivedFrom":sQuery(id+"F0.wireOp",EDGE,"E156")}),1.0]])]});
            var Q40;
            Q40=makeQuery(id+"F0.imprint","IMPRINT",FACE,{"disambiguationData":[TD([[makeQuery(id+"F0.imprint","IMPRINT",EDGE,{"derivedFrom":sQuery(id+"F0.wireOp",EDGE,"E104")}),1.0]])]});
            var Q41;
            Q41=makeQuery(id+"F0.imprint","IMPRINT",FACE,{"disambiguationData":[TD([[makeQuery(id+"F0.imprint","IMPRINT",EDGE,{"derivedFrom":sQuery(id+"F0.wireOp",EDGE,"E58")}),1.0]])]});
            var Q42;
            Q42=makeQuery(id+"F0.imprint","IMPRINT",FACE,{"disambiguationData":[TD([[makeQuery(id+"F0.imprint","IMPRINT",EDGE,{"derivedFrom":sQuery(id+"F0.wireOp",EDGE,"E6")}),1.0]])]});
            var Q43;
            Q43=makeQuery(id+"F0.imprint","IMPRINT",FACE,{"disambiguationData":[TD([[makeQuery(id+"F0.imprint","IMPRINT",EDGE,{"derivedFrom":sQuery(id+"F0.wireOp",EDGE,"E0")}),1.0]])]});
            var Q44;
            Q44=makeQuery(id+"F0.imprint","IMPRINT",FACE,{"disambiguationData":[TD([[makeQuery(id+"F0.imprint","IMPRINT",EDGE,{"derivedFrom":sQuery(id+"F0.wireOp",EDGE,"E12")}),1.0]])]});
            var Q45;
            Q45=makeQuery(id+"F0.imprint","IMPRINT",FACE,{"disambiguationData":[TD([[makeQuery(id+"F0.imprint","IMPRINT",EDGE,{"derivedFrom":sQuery(id+"F0.wireOp",EDGE,"E0")}),-1.0]])]});
            var Q46;
            Q46=makeQuery(id+"F0.imprint","IMPRINT",FACE,{"disambiguationData":[TD([[makeQuery(id+"F0.imprint","IMPRINT",EDGE,{"derivedFrom":sQuery(id+"F0.wireOp",EDGE,"E161")}),1.0]])]});
            var Q47;
            Q47=makeQuery(id+"F0.imprint","IMPRINT",FACE,{"disambiguationData":[TD([[makeQuery(id+"F0.imprint","IMPRINT",EDGE,{"derivedFrom":sQuery(id+"F0.wireOp",EDGE,"E209")}),1.0]])]});
            extrude(context, id + "F1", {"entities" : qUnion([Q0, Q1, Q2, Q3, Q4, Q5, Q6, Q7, Q8, Q9, Q10, Q11, Q12, Q13, Q14, Q15, Q16, Q17, Q18, Q19, Q20, Q21, Q22, Q23, Q24, Q25, Q26, Q27, Q28, Q29, Q30, Q31, Q32, Q33, Q34, Q35, Q36, Q37, Q38, Q39, Q40, Q41, Q42, Q43, Q44, Q45, Q46, Q47]), "depth" : 25.4 * mm, "offsetDistance" : 25.4 * mm});
        }
        {
            var Q0;
            Q0=makeQuery(id+"F0.imprint","IMPRINT",FACE,{"disambiguationData":[TD([[makeQuery(id+"F0.imprint","IMPRINT",EDGE,{"derivedFrom":sQuery(id+"F0.wireOp",EDGE,"E98")}),1.0]])]});
            var Q1;
            Q1=makeQuery(id+"F0.imprint","IMPRINT",FACE,{"disambiguationData":[TD([[makeQuery(id+"F0.imprint","IMPRINT",EDGE,{"derivedFrom":sQuery(id+"F0.wireOp",EDGE,"E46")}),1.0]])]});
            var Q2;
            Q2=makeQuery(id+"F0.imprint","IMPRINT",FACE,{"disambiguationData":[TD([[makeQuery(id+"F0.imprint","IMPRINT",EDGE,{"derivedFrom":sQuery(id+"F0.wireOp",EDGE,"E52")}),1.0]])]});
            var Q3;
            Q3=makeQuery(id+"F0.imprint","IMPRINT",FACE,{"disambiguationData":[TD([[makeQuery(id+"F0.imprint","IMPRINT",EDGE,{"derivedFrom":sQuery(id+"F0.wireOp",EDGE,"E92")}),1.0]])]});
            var Q4;
            Q4=makeQuery(id+"F0.imprint","IMPRINT",FACE,{"disambiguationData":[TD([[makeQuery(id+"F0.imprint","IMPRINT",EDGE,{"derivedFrom":sQuery(id+"F0.wireOp",EDGE,"E80")}),1.0]])]});
            var Q5;
            Q5=makeQuery(id+"F0.imprint","IMPRINT",FACE,{"disambiguationData":[TD([[makeQuery(id+"F0.imprint","IMPRINT",EDGE,{"derivedFrom":sQuery(id+"F0.wireOp",EDGE,"E74")}),1.0]])]});
            var Q6;
            Q6=makeQuery(id+"F0.imprint","IMPRINT",FACE,{"disambiguationData":[TD([[makeQuery(id+"F0.imprint","IMPRINT",EDGE,{"derivedFrom":sQuery(id+"F0.wireOp",EDGE,"E86")}),1.0]])]});
            var Q7;
            Q7=makeQuery(id+"F0.imprint","IMPRINT",FACE,{"disambiguationData":[TD([[makeQuery(id+"F0.imprint","IMPRINT",EDGE,{"derivedFrom":sQuery(id+"F0.wireOp",EDGE,"E68")}),1.0]])]});
            var Q8;
            Q8=makeQuery(id+"F0.imprint","IMPRINT",FACE,{"disambiguationData":[TD([[makeQuery(id+"F0.imprint","IMPRINT",EDGE,{"derivedFrom":sQuery(id+"F0.wireOp",EDGE,"E114")}),1.0]])]});
            var Q9;
            Q9=makeQuery(id+"F0.imprint","IMPRINT",FACE,{"disambiguationData":[TD([[makeQuery(id+"F0.imprint","IMPRINT",EDGE,{"derivedFrom":sQuery(id+"F0.wireOp",EDGE,"E120")}),1.0]])]});
            var Q10;
            Q10=makeQuery(id+"F0.imprint","IMPRINT",FACE,{"disambiguationData":[TD([[makeQuery(id+"F0.imprint","IMPRINT",EDGE,{"derivedFrom":sQuery(id+"F0.wireOp",EDGE,"E126")}),1.0]])]});
            var Q11;
            Q11=makeQuery(id+"F0.imprint","IMPRINT",FACE,{"disambiguationData":[TD([[makeQuery(id+"F0.imprint","IMPRINT",EDGE,{"derivedFrom":sQuery(id+"F0.wireOp",EDGE,"E132")}),1.0]])]});
            var Q12;
            Q12=makeQuery(id+"F0.imprint","IMPRINT",FACE,{"disambiguationData":[TD([[makeQuery(id+"F0.imprint","IMPRINT",EDGE,{"derivedFrom":sQuery(id+"F0.wireOp",EDGE,"E138")}),1.0]])]});
            var Q13;
            Q13=makeQuery(id+"F0.imprint","IMPRINT",FACE,{"disambiguationData":[TD([[makeQuery(id+"F0.imprint","IMPRINT",EDGE,{"derivedFrom":sQuery(id+"F0.wireOp",EDGE,"E144")}),1.0]])]});
            var Q14;
            Q14=makeQuery(id+"F0.imprint","IMPRINT",FACE,{"disambiguationData":[TD([[makeQuery(id+"F0.imprint","IMPRINT",EDGE,{"derivedFrom":sQuery(id+"F0.wireOp",EDGE,"E150")}),1.0]])]});
            var Q15;
            Q15=makeQuery(id+"F0.imprint","IMPRINT",FACE,{"disambiguationData":[TD([[makeQuery(id+"F0.imprint","IMPRINT",EDGE,{"derivedFrom":sQuery(id+"F0.wireOp",EDGE,"E197")}),1.0]])]});
            var Q16;
            Q16=makeQuery(id+"F0.imprint","IMPRINT",FACE,{"disambiguationData":[TD([[makeQuery(id+"F0.imprint","IMPRINT",EDGE,{"derivedFrom":sQuery(id+"F0.wireOp",EDGE,"E191")}),1.0]])]});
            var Q17;
            Q17=makeQuery(id+"F0.imprint","IMPRINT",FACE,{"disambiguationData":[TD([[makeQuery(id+"F0.imprint","IMPRINT",EDGE,{"derivedFrom":sQuery(id+"F0.wireOp",EDGE,"E179")}),1.0]])]});
            var Q18;
            Q18=makeQuery(id+"F0.imprint","IMPRINT",FACE,{"disambiguationData":[TD([[makeQuery(id+"F0.imprint","IMPRINT",EDGE,{"derivedFrom":sQuery(id+"F0.wireOp",EDGE,"E173")}),1.0]])]});
            var Q19;
            Q19=makeQuery(id+"F0.imprint","IMPRINT",FACE,{"disambiguationData":[TD([[makeQuery(id+"F0.imprint","IMPRINT",EDGE,{"derivedFrom":sQuery(id+"F0.wireOp",EDGE,"E185")}),1.0]])]});
            var Q20;
            Q20=makeQuery(id+"F0.imprint","IMPRINT",FACE,{"disambiguationData":[TD([[makeQuery(id+"F0.imprint","IMPRINT",EDGE,{"derivedFrom":sQuery(id+"F0.wireOp",EDGE,"E167")}),1.0]])]});
            var Q21;
            Q21=makeQuery(id+"F0.imprint","IMPRINT",FACE,{"disambiguationData":[TD([[makeQuery(id+"F0.imprint","IMPRINT",EDGE,{"derivedFrom":sQuery(id+"F0.wireOp",EDGE,"E28")}),1.0]])]});
            var Q22;
            Q22=makeQuery(id+"F0.imprint","IMPRINT",FACE,{"disambiguationData":[TD([[makeQuery(id+"F0.imprint","IMPRINT",EDGE,{"derivedFrom":sQuery(id+"F0.wireOp",EDGE,"E22")}),1.0]])]});
            var Q23;
            Q23=makeQuery(id+"F0.imprint","IMPRINT",FACE,{"disambiguationData":[TD([[makeQuery(id+"F0.imprint","IMPRINT",EDGE,{"derivedFrom":sQuery(id+"F0.wireOp",EDGE,"E16")}),1.0]])]});
            extrude(context, id + "F2", {"entities" : qUnion([Q0, Q1, Q2, Q3, Q4, Q5, Q6, Q7, Q8, Q9, Q10, Q11, Q12, Q13, Q14, Q15, Q16, Q17, Q18, Q19, Q20, Q21, Q22, Q23]), "operationType" : NewBodyOperationType.REMOVE, "depth" : 25.4 * mm, "offsetDistance" : 25.4 * mm});
        }
        {
            var Q0;
            Q0=makeQuery(id+"F0.imprint","IMPRINT",FACE,{"disambiguationData":[TD([[makeQuery(id+"F0.imprint","IMPRINT",EDGE,{"derivedFrom":sQuery(id+"F0.wireOp",EDGE,"E58")}),1.0]])]});
            var Q1;
            Q1=makeQuery(id+"F0.imprint","IMPRINT",FACE,{"disambiguationData":[TD([[makeQuery(id+"F0.imprint","IMPRINT",EDGE,{"derivedFrom":sQuery(id+"F0.wireOp",EDGE,"E156")}),1.0]])]});
            var Q2;
            Q2=makeQuery(id+"F0.imprint","IMPRINT",FACE,{"disambiguationData":[TD([[makeQuery(id+"F0.imprint","IMPRINT",EDGE,{"derivedFrom":sQuery(id+"F0.wireOp",EDGE,"E213")}),1.0]])]});
            var Q3;
            Q3=makeQuery(id+"F0.imprint","IMPRINT",FACE,{"disambiguationData":[TD([[makeQuery(id+"F0.imprint","IMPRINT",EDGE,{"derivedFrom":sQuery(id+"F0.wireOp",EDGE,"E209")}),1.0]])]});
            var Q4;
            Q4=makeQuery(id+"F0.imprint","IMPRINT",FACE,{"disambiguationData":[TD([[makeQuery(id+"F0.imprint","IMPRINT",EDGE,{"derivedFrom":sQuery(id+"F0.wireOp",EDGE,"E12")}),1.0]])]});
            var Q5;
            Q5=makeQuery(id+"F0.imprint","IMPRINT",FACE,{"disambiguationData":[TD([[makeQuery(id+"F0.imprint","IMPRINT",EDGE,{"derivedFrom":sQuery(id+"F0.wireOp",EDGE,"E104")}),1.0]])]});
            var Q6;
            Q6=makeQuery(id+"F0.imprint","IMPRINT",FACE,{"disambiguationData":[TD([[makeQuery(id+"F0.imprint","IMPRINT",EDGE,{"derivedFrom":sQuery(id+"F0.wireOp",EDGE,"E203")}),1.0]])]});
            var Q7;
            Q7=makeQuery(id+"F0.imprint","IMPRINT",FACE,{"disambiguationData":[TD([[makeQuery(id+"F0.imprint","IMPRINT",EDGE,{"derivedFrom":sQuery(id+"F0.wireOp",EDGE,"E161")}),1.0]])]});
            var Q8;
            Q8=makeQuery(id+"F0.imprint","IMPRINT",FACE,{"disambiguationData":[TD([[makeQuery(id+"F0.imprint","IMPRINT",EDGE,{"derivedFrom":sQuery(id+"F0.wireOp",EDGE,"E0")}),1.0]])]});
            var Q9;
            Q9=makeQuery(id+"F0.imprint","IMPRINT",FACE,{"disambiguationData":[TD([[makeQuery(id+"F0.imprint","IMPRINT",EDGE,{"derivedFrom":sQuery(id+"F0.wireOp",EDGE,"E6")}),1.0]])]});
            extrude(context, id + "F3", {"entities" : qUnion([Q0, Q1, Q2, Q3, Q4, Q5, Q6, Q7, Q8, Q9]), "operationType" : NewBodyOperationType.REMOVE, "depth" : 25.4 * mm, "offsetDistance" : 25.4 * mm});
        }
        {
            var Q0;
            Q0=makeQuery(id+"F0.imprint","IMPRINT",FACE,{"disambiguationData":[TD([[makeQuery(id+"F0.imprint","IMPRINT",EDGE,{"derivedFrom":sQuery(id+"F0.wireOp",EDGE,"E0")}),-1.0]])]});
            var sketch = newSketch(context, id + "F4", { "sketchPlane" : qUnion([Q0])});
            skLineSegment(sketch, "E227", {"start": v(37.49, -51.28) * mm, "end": v(32.4, -42.48) * mm});
            skLineSegment(sketch, "E228", {"start": v(32.4, -42.48) * mm, "end": v(37.49, -33.69) * mm});
            skLineSegment(sketch, "E229", {"start": v(37.49, -33.69) * mm, "end": v(47.65, -33.69) * mm});
            skLineSegment(sketch, "E230", {"start": v(47.65, -33.69) * mm, "end": v(52.73, -42.48) * mm});
            skLineSegment(sketch, "E231", {"start": v(52.73, -42.48) * mm, "end": v(47.65, -51.28) * mm});
            skLineSegment(sketch, "E232", {"start": v(47.65, -51.28) * mm, "end": v(37.49, -51.28) * mm});
            skLineSegment(sketch, "E233", {"start": v(37.49, -29.88) * mm, "end": v(32.4, -21.08) * mm});
            skLineSegment(sketch, "E234", {"start": v(32.4, -21.08) * mm, "end": v(37.49, -12.28) * mm});
            skLineSegment(sketch, "E235", {"start": v(37.49, -12.28) * mm, "end": v(47.65, -12.28) * mm});
            skLineSegment(sketch, "E236", {"start": v(47.65, -12.28) * mm, "end": v(52.73, -21.08) * mm});
            skLineSegment(sketch, "E237", {"start": v(52.73, -21.08) * mm, "end": v(47.65, -29.88) * mm});
            skLineSegment(sketch, "E238", {"start": v(47.65, -29.88) * mm, "end": v(37.49, -29.88) * mm});
            skLineSegment(sketch, "E239", {"start": v(37.49, -8.47) * mm, "end": v(32.4, 0.33) * mm});
            skLineSegment(sketch, "E240", {"start": v(32.4, 0.33) * mm, "end": v(37.49, 9.13) * mm});
            skLineSegment(sketch, "E241", {"start": v(37.49, 9.13) * mm, "end": v(47.65, 9.13) * mm});
            skLineSegment(sketch, "E242", {"start": v(47.65, 9.13) * mm, "end": v(52.73, 0.33) * mm});
            skLineSegment(sketch, "E243", {"start": v(52.73, 0.33) * mm, "end": v(47.65, -8.47) * mm});
            skLineSegment(sketch, "E244", {"start": v(47.65, -8.47) * mm, "end": v(37.49, -8.47) * mm});
            skLineSegment(sketch, "E245", {"start": v(37.49, 12.94) * mm, "end": v(32.4, 21.74) * mm});
            skLineSegment(sketch, "E246", {"start": v(32.4, 21.74) * mm, "end": v(37.49, 30.54) * mm});
            skLineSegment(sketch, "E247", {"start": v(37.49, 30.54) * mm, "end": v(47.65, 30.54) * mm});
            skLineSegment(sketch, "E248", {"start": v(47.65, 30.54) * mm, "end": v(52.73, 21.74) * mm});
            skLineSegment(sketch, "E249", {"start": v(52.73, 21.74) * mm, "end": v(47.65, 12.94) * mm});
            skLineSegment(sketch, "E250", {"start": v(47.65, 12.94) * mm, "end": v(37.49, 12.94) * mm});
            skLineSegment(sketch, "E251", {"start": v(37.49, 34.35) * mm, "end": v(32.4, 43.15) * mm});
            skLineSegment(sketch, "E252", {"start": v(32.4, 43.15) * mm, "end": v(37.49, 51.95) * mm});
            skLineSegment(sketch, "E253", {"start": v(37.49, 51.95) * mm, "end": v(47.65, 51.95) * mm});
            skLineSegment(sketch, "E254", {"start": v(47.65, 51.95) * mm, "end": v(52.73, 43.15) * mm});
            skLineSegment(sketch, "E255", {"start": v(52.73, 43.15) * mm, "end": v(47.65, 34.35) * mm});
            skLineSegment(sketch, "E256", {"start": v(47.65, 34.35) * mm, "end": v(37.49, 34.35) * mm});
            skLineSegment(sketch, "E257", {"start": v(37.49, 55.76) * mm, "end": v(32.4, 64.55) * mm});
            skLineSegment(sketch, "E258", {"start": v(32.4, 64.55) * mm, "end": v(37.49, 73.35) * mm});
            skLineSegment(sketch, "E259", {"start": v(37.49, 73.35) * mm, "end": v(47.65, 73.35) * mm});
            skLineSegment(sketch, "E260", {"start": v(47.65, 73.35) * mm, "end": v(52.73, 64.55) * mm});
            skLineSegment(sketch, "E261", {"start": v(52.73, 64.55) * mm, "end": v(47.65, 55.76) * mm});
            skLineSegment(sketch, "E262", {"start": v(47.65, 55.76) * mm, "end": v(37.49, 55.76) * mm});
            skLineSegment(sketch, "E263", {"start": v(37.49, 77.16) * mm, "end": v(32.4, 85.96) * mm});
            skLineSegment(sketch, "E264", {"start": v(32.4, 85.96) * mm, "end": v(37.49, 94.76) * mm});
            skLineSegment(sketch, "E265", {"start": v(37.49, 94.76) * mm, "end": v(47.65, 94.76) * mm});
            skLineSegment(sketch, "E266", {"start": v(47.65, 94.76) * mm, "end": v(52.73, 85.96) * mm});
            skLineSegment(sketch, "E267", {"start": v(52.73, 85.96) * mm, "end": v(47.65, 77.16) * mm});
            skLineSegment(sketch, "E268", {"start": v(47.65, 77.16) * mm, "end": v(37.49, 77.16) * mm});
            skLineSegment(sketch, "E269", {"start": v(-64.11, -38.67) * mm, "end": v(-69.2, -29.88) * mm});
            skLineSegment(sketch, "E270", {"start": v(-69.2, -29.88) * mm, "end": v(-64.11, -21.08) * mm});
            skLineSegment(sketch, "E271", {"start": v(-64.11, -21.08) * mm, "end": v(-53.95, -21.08) * mm});
            skLineSegment(sketch, "E272", {"start": v(-53.95, -21.08) * mm, "end": v(-48.87, -29.88) * mm});
            skLineSegment(sketch, "E273", {"start": v(-48.87, -29.88) * mm, "end": v(-53.95, -38.67) * mm});
            skLineSegment(sketch, "E274", {"start": v(-53.95, -38.67) * mm, "end": v(-64.11, -38.67) * mm});
            skLineSegment(sketch, "E275", {"start": v(-64.11, -17.27) * mm, "end": v(-69.2, -8.47) * mm});
            skLineSegment(sketch, "E276", {"start": v(-69.2, -8.47) * mm, "end": v(-64.11, 0.33) * mm});
            skLineSegment(sketch, "E277", {"start": v(-64.11, 0.33) * mm, "end": v(-53.95, 0.33) * mm});
            skLineSegment(sketch, "E278", {"start": v(-53.95, 0.33) * mm, "end": v(-48.87, -8.47) * mm});
            skLineSegment(sketch, "E279", {"start": v(-48.87, -8.47) * mm, "end": v(-53.95, -17.27) * mm});
            skLineSegment(sketch, "E280", {"start": v(-53.95, -17.27) * mm, "end": v(-64.11, -17.27) * mm});
            skLineSegment(sketch, "E281", {"start": v(-64.11, 4.14) * mm, "end": v(-69.2, 12.94) * mm});
            skLineSegment(sketch, "E282", {"start": v(-69.2, 12.94) * mm, "end": v(-64.11, 21.74) * mm});
            skLineSegment(sketch, "E283", {"start": v(-64.11, 21.74) * mm, "end": v(-53.95, 21.74) * mm});
            skLineSegment(sketch, "E284", {"start": v(-53.95, 21.74) * mm, "end": v(-48.87, 12.94) * mm});
            skLineSegment(sketch, "E285", {"start": v(-48.87, 12.94) * mm, "end": v(-53.95, 4.14) * mm});
            skLineSegment(sketch, "E286", {"start": v(-53.95, 4.14) * mm, "end": v(-64.11, 4.14) * mm});
            skLineSegment(sketch, "E287", {"start": v(-64.11, 25.55) * mm, "end": v(-69.2, 34.35) * mm});
            skLineSegment(sketch, "E288", {"start": v(-69.2, 34.35) * mm, "end": v(-64.11, 43.15) * mm});
            skLineSegment(sketch, "E289", {"start": v(-64.11, 43.15) * mm, "end": v(-53.95, 43.15) * mm});
            skLineSegment(sketch, "E290", {"start": v(-53.95, 43.15) * mm, "end": v(-48.87, 34.35) * mm});
            skLineSegment(sketch, "E291", {"start": v(-48.87, 34.35) * mm, "end": v(-53.95, 25.55) * mm});
            skLineSegment(sketch, "E292", {"start": v(-53.95, 25.55) * mm, "end": v(-64.11, 25.55) * mm});
            skLineSegment(sketch, "E293", {"start": v(-64.11, 46.96) * mm, "end": v(-69.2, 55.76) * mm});
            skLineSegment(sketch, "E294", {"start": v(-69.2, 55.76) * mm, "end": v(-64.11, 64.55) * mm});
            skLineSegment(sketch, "E295", {"start": v(-64.11, 64.55) * mm, "end": v(-53.95, 64.55) * mm});
            skLineSegment(sketch, "E296", {"start": v(-53.95, 64.55) * mm, "end": v(-48.87, 55.76) * mm});
            skLineSegment(sketch, "E297", {"start": v(-48.87, 55.76) * mm, "end": v(-53.95, 46.96) * mm});
            skLineSegment(sketch, "E298", {"start": v(-53.95, 46.96) * mm, "end": v(-64.11, 46.96) * mm});
            skLineSegment(sketch, "E299", {"start": v(-64.11, 68.36) * mm, "end": v(-69.2, 77.16) * mm});
            skLineSegment(sketch, "E300", {"start": v(-69.2, 77.16) * mm, "end": v(-64.11, 85.96) * mm});
            skLineSegment(sketch, "E301", {"start": v(-64.11, 85.96) * mm, "end": v(-53.95, 85.96) * mm});
            skLineSegment(sketch, "E302", {"start": v(-53.95, 85.96) * mm, "end": v(-48.87, 77.16) * mm});
            skLineSegment(sketch, "E303", {"start": v(-48.87, 77.16) * mm, "end": v(-53.95, 68.36) * mm});
            skLineSegment(sketch, "E304", {"start": v(-53.95, 68.36) * mm, "end": v(-64.11, 68.36) * mm});
            skSolve(sketch);
        }
        {
            var Q0;
            Q0=makeQuery(id+"F4.imprint","IMPRINT",FACE,{"disambiguationData":[TD([[makeQuery(id+"F4.imprint","IMPRINT",EDGE,{"derivedFrom":sQuery(id+"F4.wireOp",EDGE,"E227")}),-1.0]])]});
            var Q1;
            Q1=makeQuery(id+"F4.imprint","IMPRINT",FACE,{"disambiguationData":[TD([[makeQuery(id+"F4.imprint","IMPRINT",EDGE,{"derivedFrom":sQuery(id+"F4.wireOp",EDGE,"E233")}),-1.0]])]});
            var Q2;
            Q2=makeQuery(id+"F4.imprint","IMPRINT",FACE,{"disambiguationData":[TD([[makeQuery(id+"F4.imprint","IMPRINT",EDGE,{"derivedFrom":sQuery(id+"F4.wireOp",EDGE,"E239")}),-1.0]])]});
            var Q3;
            Q3=makeQuery(id+"F4.imprint","IMPRINT",FACE,{"disambiguationData":[TD([[makeQuery(id+"F4.imprint","IMPRINT",EDGE,{"derivedFrom":sQuery(id+"F4.wireOp",EDGE,"E245")}),-1.0]])]});
            var Q4;
            Q4=makeQuery(id+"F4.imprint","IMPRINT",FACE,{"disambiguationData":[TD([[makeQuery(id+"F4.imprint","IMPRINT",EDGE,{"derivedFrom":sQuery(id+"F4.wireOp",EDGE,"E251")}),-1.0]])]});
            var Q5;
            Q5=makeQuery(id+"F4.imprint","IMPRINT",FACE,{"disambiguationData":[TD([[makeQuery(id+"F4.imprint","IMPRINT",EDGE,{"derivedFrom":sQuery(id+"F4.wireOp",EDGE,"E257")}),-1.0]])]});
            var Q6;
            Q6=makeQuery(id+"F4.imprint","IMPRINT",FACE,{"disambiguationData":[TD([[makeQuery(id+"F4.imprint","IMPRINT",EDGE,{"derivedFrom":sQuery(id+"F4.wireOp",EDGE,"E263")}),-1.0]])]});
            var Q7;
            Q7=makeQuery(id+"F4.imprint","IMPRINT",FACE,{"disambiguationData":[TD([[makeQuery(id+"F4.imprint","IMPRINT",EDGE,{"derivedFrom":sQuery(id+"F4.wireOp",EDGE,"E299")}),-1.0]])]});
            var Q8;
            Q8=makeQuery(id+"F4.imprint","IMPRINT",FACE,{"disambiguationData":[TD([[makeQuery(id+"F4.imprint","IMPRINT",EDGE,{"derivedFrom":sQuery(id+"F4.wireOp",EDGE,"E293")}),-1.0]])]});
            var Q9;
            Q9=makeQuery(id+"F4.imprint","IMPRINT",FACE,{"disambiguationData":[TD([[makeQuery(id+"F4.imprint","IMPRINT",EDGE,{"derivedFrom":sQuery(id+"F4.wireOp",EDGE,"E287")}),-1.0]])]});
            var Q10;
            Q10=makeQuery(id+"F4.imprint","IMPRINT",FACE,{"disambiguationData":[TD([[makeQuery(id+"F4.imprint","IMPRINT",EDGE,{"derivedFrom":sQuery(id+"F4.wireOp",EDGE,"E281")}),-1.0]])]});
            var Q11;
            Q11=makeQuery(id+"F4.imprint","IMPRINT",FACE,{"disambiguationData":[TD([[makeQuery(id+"F4.imprint","IMPRINT",EDGE,{"derivedFrom":sQuery(id+"F4.wireOp",EDGE,"E275")}),-1.0]])]});
            var Q12;
            Q12=makeQuery(id+"F4.imprint","IMPRINT",FACE,{"disambiguationData":[TD([[makeQuery(id+"F4.imprint","IMPRINT",EDGE,{"derivedFrom":sQuery(id+"F4.wireOp",EDGE,"E269")}),-1.0]])]});
            extrude(context, id + "F5", {"entities" : qUnion([Q0, Q1, Q2, Q3, Q4, Q5, Q6, Q7, Q8, Q9, Q10, Q11, Q12]), "operationType" : NewBodyOperationType.REMOVE, "depth" : 25.4 * mm, "offsetDistance" : 25.4 * mm});
        }
        {
            var Q0;
            Q0=makeQuery(id+"F0.imprint","IMPRINT",FACE,{"disambiguationData":[TD([[makeQuery(id+"F0.imprint","IMPRINT",EDGE,{"derivedFrom":sQuery(id+"F0.wireOp",EDGE,"E219.bottom")}),-1.0]])]});
            extrude(context, id + "F6", {"entities" : qUnion([Q0]), "operationType" : NewBodyOperationType.ADD, "depth" : 25.4 * mm, "offsetDistance" : 25.4 * mm});
        }
        {
            var Q0;
            {var subQ0=sQuery(id+"F0.wireOp",EDGE,"E220.right");var subQ1=sQuery(id+"F0.wireOp",EDGE,"E220.left");var subQ2=sQuery(id+"F0.wireOp",EDGE,"E220.bottom");var subQ3=sQuery(id+"F0.wireOp",EDGE,"E219.top");Q0=makeQuery(id+"F6.boolean.opBoolean","MERGE",FACE,{"derivedFrom":[makeQuery(id+"F1.opExtrude","CAP_FACE",FACE,{"disambiguationData":[OSD([sQuery(id+"F0.wireOp",EDGE,"E34"),sQuery(id+"F0.wireOp",EDGE,"E35"),sQuery(id+"F0.wireOp",EDGE,"E36"),sQuery(id+"F0.wireOp",EDGE,"E37"),sQuery(id+"F0.wireOp",EDGE,"E38"),sQuery(id+"F0.wireOp",EDGE,"E39"),sQuery(id+"F0.wireOp",EDGE,"E40"),sQuery(id+"F0.wireOp",EDGE,"E41"),sQuery(id+"F0.wireOp",EDGE,"E42"),sQuery(id+"F0.wireOp",EDGE,"E43"),sQuery(id+"F0.wireOp",EDGE,"E44"),sQuery(id+"F0.wireOp",EDGE,"E45"),sQuery(id+"F0.wireOp",EDGE,"E62"),sQuery(id+"F0.wireOp",EDGE,"E63"),sQuery(id+"F0.wireOp",EDGE,"E64"),sQuery(id+"F0.wireOp",EDGE,"E65"),sQuery(id+"F0.wireOp",EDGE,"E66"),sQuery(id+"F0.wireOp",EDGE,"E67"),sQuery(id+"F0.wireOp",EDGE,"E110"),sQuery(id+"F0.wireOp",EDGE,"E111"),sQuery(id+"F0.wireOp",EDGE,"E112"),subQ3,subQ2,subQ1,subQ0,sQuery(id+"F0.wireOp",EDGE,"E224")])],"isStart":false}),makeQuery(id+"F6.opExtrude","CAP_FACE",FACE,{"disambiguationData":[OSD([sQuery(id+"F0.wireOp",EDGE,"E219.bottom"),subQ3,sQuery(id+"F0.wireOp",EDGE,"E219.left"),sQuery(id+"F0.wireOp",EDGE,"E219.right"),subQ2,subQ1,subQ0])],"isStart":false})]});}
            var sketch = newSketch(context, id + "F7", { "sketchPlane" : qUnion([Q0])});
            skLineSegment(sketch, "E305.bottom", {"start": v(-74.27, 89.59) * mm, "end": v(-71.73, 89.59) * mm});
            skLineSegment(sketch, "E305.top", {"start": v(-74.27, 76.89) * mm, "end": v(-71.73, 76.89) * mm});
            skLineSegment(sketch, "E305.left", {"start": v(-74.27, 89.59) * mm, "end": v(-74.27, 76.89) * mm});
            skLineSegment(sketch, "E305.right", {"start": v(-71.73, 89.59) * mm, "end": v(-71.73, 76.89) * mm});
            skLineSegment(sketch, "E306.bottom", {"start": v(-74.27, -29.8) * mm, "end": v(-71.73, -29.8) * mm});
            skLineSegment(sketch, "E306.top", {"start": v(-74.27, -42.5) * mm, "end": v(-71.73, -42.5) * mm});
            skLineSegment(sketch, "E306.left", {"start": v(-74.27, -29.8) * mm, "end": v(-74.27, -42.5) * mm});
            skLineSegment(sketch, "E306.right", {"start": v(-71.73, -29.8) * mm, "end": v(-71.73, -42.5) * mm});
            skLineSegment(sketch, "E307.bottom", {"start": v(-74.27, 31.17) * mm, "end": v(-71.73, 31.17) * mm});
            skLineSegment(sketch, "E307.top", {"start": v(-74.27, 18.47) * mm, "end": v(-71.73, 18.47) * mm});
            skLineSegment(sketch, "E307.left", {"start": v(-74.27, 31.17) * mm, "end": v(-74.27, 18.47) * mm});
            skLineSegment(sketch, "E307.right", {"start": v(-71.73, 31.17) * mm, "end": v(-71.73, 18.47) * mm});
            skLineSegment(sketch, "E308.bottom", {"start": v(55.27, 89.59) * mm, "end": v(57.8, 89.59) * mm});
            skLineSegment(sketch, "E308.top", {"start": v(55.27, 76.89) * mm, "end": v(57.8, 76.89) * mm});
            skLineSegment(sketch, "E308.left", {"start": v(55.27, 89.59) * mm, "end": v(55.27, 76.89) * mm});
            skLineSegment(sketch, "E308.right", {"start": v(57.8, 89.59) * mm, "end": v(57.8, 76.89) * mm});
            skLineSegment(sketch, "E309.bottom", {"start": v(55.27, 31.17) * mm, "end": v(57.8, 31.17) * mm});
            skLineSegment(sketch, "E309.top", {"start": v(55.27, 18.47) * mm, "end": v(57.8, 18.47) * mm});
            skLineSegment(sketch, "E309.left", {"start": v(55.27, 31.17) * mm, "end": v(55.27, 18.47) * mm});
            skLineSegment(sketch, "E309.right", {"start": v(57.8, 31.17) * mm, "end": v(57.8, 18.47) * mm});
            skLineSegment(sketch, "E310.bottom", {"start": v(55.27, -29.8) * mm, "end": v(57.8, -29.8) * mm});
            skLineSegment(sketch, "E310.top", {"start": v(55.27, -42.5) * mm, "end": v(57.8, -42.5) * mm});
            skLineSegment(sketch, "E310.left", {"start": v(55.27, -29.8) * mm, "end": v(55.27, -42.5) * mm});
            skLineSegment(sketch, "E310.right", {"start": v(57.8, -29.8) * mm, "end": v(57.8, -42.5) * mm});
            skLineSegment(sketch, "E311.bottom", {"start": v(-51.41, 112.45) * mm, "end": v(-38.71, 112.45) * mm});
            skLineSegment(sketch, "E311.top", {"start": v(-51.41, 109.9) * mm, "end": v(-38.71, 109.9) * mm});
            skLineSegment(sketch, "E311.left", {"start": v(-51.41, 112.45) * mm, "end": v(-51.41, 109.9) * mm});
            skLineSegment(sketch, "E311.right", {"start": v(-38.71, 112.45) * mm, "end": v(-38.71, 109.9) * mm});
            skLineSegment(sketch, "E312.bottom", {"start": v(22.25, 112.45) * mm, "end": v(34.95, 112.45) * mm});
            skLineSegment(sketch, "E312.top", {"start": v(22.25, 109.9) * mm, "end": v(34.95, 109.9) * mm});
            skLineSegment(sketch, "E312.left", {"start": v(22.25, 112.45) * mm, "end": v(22.25, 109.9) * mm});
            skLineSegment(sketch, "E312.right", {"start": v(34.95, 112.45) * mm, "end": v(34.95, 109.9) * mm});
            skSolve(sketch);
        }
        {
            var Q0;
            Q0=makeQuery(id+"F7.imprint","IMPRINT",FACE,{"disambiguationData":[TD([[makeQuery(id+"F7.imprint","IMPRINT",EDGE,{"derivedFrom":sQuery(id+"F7.wireOp",EDGE,"E306.bottom")}),-1.0]])]});
            var Q1;
            Q1=makeQuery(id+"F7.imprint","IMPRINT",FACE,{"disambiguationData":[TD([[makeQuery(id+"F7.imprint","IMPRINT",EDGE,{"derivedFrom":sQuery(id+"F7.wireOp",EDGE,"E307.bottom")}),-1.0]])]});
            var Q2;
            Q2=makeQuery(id+"F7.imprint","IMPRINT",FACE,{"disambiguationData":[TD([[makeQuery(id+"F7.imprint","IMPRINT",EDGE,{"derivedFrom":sQuery(id+"F7.wireOp",EDGE,"E310.bottom")}),-1.0]])]});
            var Q3;
            Q3=makeQuery(id+"F7.imprint","IMPRINT",FACE,{"disambiguationData":[TD([[makeQuery(id+"F7.imprint","IMPRINT",EDGE,{"derivedFrom":sQuery(id+"F7.wireOp",EDGE,"E309.bottom")}),-1.0]])]});
            var Q4;
            Q4=makeQuery(id+"F7.imprint","IMPRINT",FACE,{"disambiguationData":[TD([[makeQuery(id+"F7.imprint","IMPRINT",EDGE,{"derivedFrom":sQuery(id+"F7.wireOp",EDGE,"E305.bottom")}),-1.0]])]});
            var Q5;
            Q5=makeQuery(id+"F7.imprint","IMPRINT",FACE,{"disambiguationData":[TD([[makeQuery(id+"F7.imprint","IMPRINT",EDGE,{"derivedFrom":sQuery(id+"F7.wireOp",EDGE,"E308.bottom")}),-1.0]])]});
            var Q6;
            Q6=makeQuery(id+"F7.imprint","IMPRINT",FACE,{"disambiguationData":[TD([[makeQuery(id+"F7.imprint","IMPRINT",EDGE,{"derivedFrom":sQuery(id+"F7.wireOp",EDGE,"E311.bottom")}),-1.0]])]});
            var Q7;
            Q7=makeQuery(id+"F7.imprint","IMPRINT",FACE,{"disambiguationData":[TD([[makeQuery(id+"F7.imprint","IMPRINT",EDGE,{"derivedFrom":sQuery(id+"F7.wireOp",EDGE,"E312.bottom")}),-1.0]])]});
            extrude(context, id + "F8", {"entities" : qUnion([Q0, Q1, Q2, Q3, Q4, Q5, Q6, Q7]), "operationType" : NewBodyOperationType.REMOVE, "oppositeDirection" : true, "depth" : 7.62 * mm, "offsetDistance" : 25.4 * mm});
        }
    });
